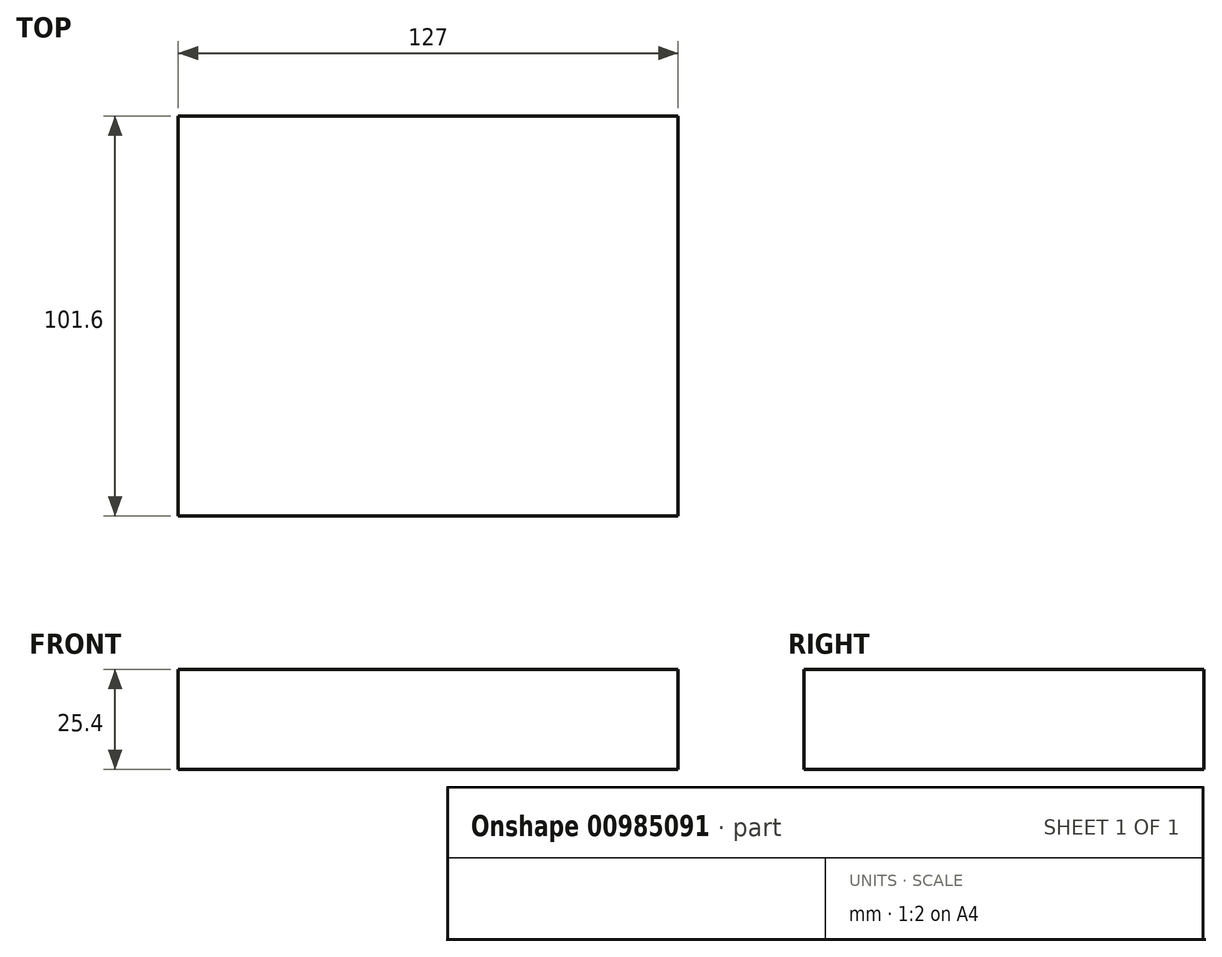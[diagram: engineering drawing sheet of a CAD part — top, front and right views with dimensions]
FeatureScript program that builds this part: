
annotation { "Feature Type Name" : "Feature", "Feature Type Description" : "" }
export const myFeature = defineFeature(function(context is Context, id is Id, definition is map)
    precondition{}
    {
        {
            var Q0;
            Q0=qCreatedBy(makeId("Top.planeOp"),FACE);
            var sketch = newSketch(context, id + "F0", { "sketchPlane" : qUnion([Q0])});
            skLineSegment(sketch, "E0.bottom", {"start": v(-127, 0) * mm, "end": v(0, 0) * mm});
            skLineSegment(sketch, "E0.top", {"start": v(-127, 101.6) * mm, "end": v(0, 101.6) * mm});
            skLineSegment(sketch, "E0.left", {"start": v(-127, 0) * mm, "end": v(-127, 101.6) * mm});
            skLineSegment(sketch, "E0.right", {"start": v(0, 0) * mm, "end": v(0, 101.6) * mm});
            skSolve(sketch);
        }
        {
            var Q0;
            Q0=makeQuery(id+"F0.imprint","IMPRINT",FACE,{"disambiguationData":[TD([[makeQuery(id+"F0.imprint","IMPRINT",EDGE,{"derivedFrom":sQuery(id+"F0.wireOp",EDGE,"E0.bottom")}),1.0]])]});
            extrude(context, id + "F1", {"entities" : qUnion([Q0]), "depth" : 25.4 * mm, "offsetDistance" : 25.4 * mm});
        }
    });
